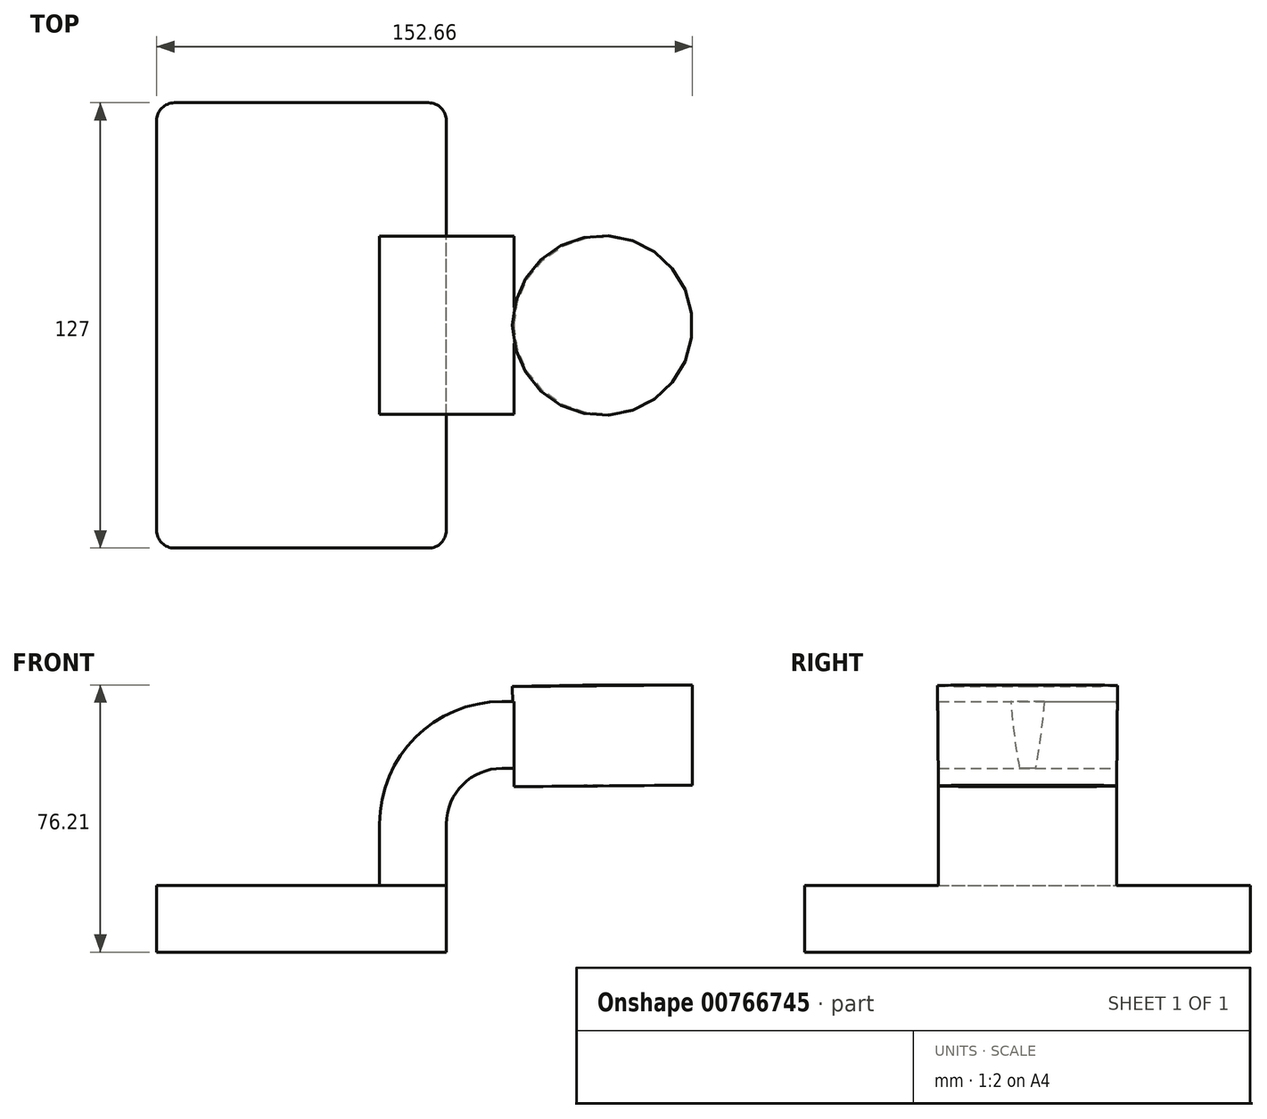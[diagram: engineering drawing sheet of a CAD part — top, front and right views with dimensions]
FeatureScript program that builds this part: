
annotation { "Feature Type Name" : "Feature", "Feature Type Description" : "" }
export const myFeature = defineFeature(function(context is Context, id is Id, definition is map)
    precondition{}
    {
        {
            var Q0;
            Q0=qCreatedBy(makeId("Front.planeOp"),FACE);
            var sketch = newSketch(context, id + "F0", { "sketchPlane" : qUnion([Q0])});
            skLineSegment(sketch, "E0.bottom", {"start": v(-41.28, 9.52) * mm, "end": v(41.27, 9.53) * mm});
            skLineSegment(sketch, "E0.top", {"start": v(-41.28, -9.53) * mm, "end": v(41.28, -9.53) * mm});
            skLineSegment(sketch, "E0.left", {"start": v(-41.28, 9.52) * mm, "end": v(-41.28, -9.53) * mm});
            skLineSegment(sketch, "E0.right", {"start": v(41.27, 9.53) * mm, "end": v(41.28, -9.52) * mm});
            skPoint(sketch, "E0.middle", {"position": v(0, 0) * mm});
            skLineSegment(sketch, "E1.bottom", {"start": v(111.39, 38.1) * mm, "end": v(60.59, 38.1) * mm});
            skLineSegment(sketch, "E1.top", {"start": v(111.39, 66.68) * mm, "end": v(60.59, 66.68) * mm});
            skLineSegment(sketch, "E1.left", {"start": v(111.39, 38.1) * mm, "end": v(111.39, 66.68) * mm});
            skLineSegment(sketch, "E1.right", {"start": v(60.59, 38.1) * mm, "end": v(60.59, 66.68) * mm});
            skPoint(sketch, "E1.middle", {"position": v(85.99, 52.39) * mm});
            skLineSegment(sketch, "E2", {"start": v(41.27, 9.53) * mm, "end": v(41.27, 27) * mm});
            skArc(sketch, "E3", {"start": v(41.27, 27) * mm, "mid": v(45.92, 38.23) * mm, "end": v(57.15, 42.88) * mm});
            skLineSegment(sketch, "E4", {"start": v(57.15, 42.88) * mm, "end": v(85.72, 42.88) * mm});
            skLineSegment(sketch, "E5.0", {"start": v(57.15, 61.93) * mm, "end": v(85.72, 61.93) * mm});
            skArc(sketch, "E5.1", {"start": v(22.22, 27) * mm, "mid": v(32.45, 51.7) * mm, "end": v(57.15, 61.93) * mm});
            skLineSegment(sketch, "E5.2", {"start": v(22.22, 9.53) * mm, "end": v(22.22, 27) * mm});
            skLineSegment(sketch, "E6", {"start": v(85.99, 38.1) * mm, "end": v(85.72, 66.68) * mm});
            skFitSpline(sketch, "E7", {"points": [v(-41.28, 9.52) * mm, v(57.15, 61.93) * mm], "startDerivative": vector(41.8, 115.77) * mm, "endDerivative": vector(181.9, -4.99) * mm});
            skSolve(sketch);
        }
        {
            var Q0;
            Q0=makeQuery(id+"F0.imprint","IMPRINT",FACE,{"disambiguationData":[TD([[makeQuery(id+"F0.imprint","IMPRINT",EDGE,{"derivedFrom":sQuery(id+"F0.wireOp",EDGE,"E0.top")}),1.0]])]});
            extrude(context, id + "F1", {"entities" : qUnion([Q0]), "endBound" : BoundingType.SYMMETRIC, "depth" : 127 * mm, "offsetDistance" : 25.4 * mm});
        }
        {
            var Q0;
            {var subQ1=sQuery(id+"F0.wireOp",EDGE,"E2");Q0=makeQuery(id+"F0.imprint","IMPRINT",FACE,{"disambiguationData":[TD([[makeQuery(id+"F0.imprint","IMPRINT",EDGE,{"derivedFrom":subQ1}),1.0]])]});}
            extrude(context, id + "F2", {"entities" : qUnion([Q0]), "operationType" : NewBodyOperationType.ADD, "endBound" : BoundingType.SYMMETRIC, "depth" : 50.8 * mm, "offsetDistance" : 25.4 * mm});
        }
        {
            var Q0;
            Q0=makeQuery(id+"F0.imprint","IMPRINT",FACE,{"disambiguationData":[TD([[makeQuery(id+"F0.imprint","IMPRINT",EDGE,{"derivedFrom":sQuery(id+"F0.wireOp",EDGE,"E5.1")}),1.0]])]});
            extrude(context, id + "F3", {"entities" : qUnion([Q0]), "operationType" : NewBodyOperationType.ADD, "endBound" : BoundingType.SYMMETRIC, "depth" : 15.88 * mm, "offsetDistance" : 25.4 * mm});
        }
        {
            var Q0;
            {var subQ0=sQuery(id+"F0.wireOp",EDGE,"E1.left");Q0=makeQuery(id+"F0.imprint","IMPRINT",FACE,{"disambiguationData":[TD([[makeQuery(id+"F0.imprint","IMPRINT",EDGE,{"derivedFrom":subQ0}),1.0]])]});}
            var Q1;
            Q1=sQuery(id+"F0.wireOp",EDGE,"E6");
            revolve(context, id + "F4", {"operationType" : NewBodyOperationType.ADD, "surfaceOperationType" : NewSurfaceOperationType.NEW, "entities" : qUnion([Q0]), "axis" : qUnion([Q1]), "revolveType" : RevolveType.FULL});
        }
        {
            var Q0;
            Q0=makeQuery(id+"F1.opExtrude","CAP_EDGE",EDGE,{"disambiguationData":[OSD([sQuery(id+"F0.wireOp",EDGE,"E0.right")])],"isStart":false});
            var Q1;
            Q1=makeQuery(id+"F1.opExtrude","CAP_EDGE",EDGE,{"disambiguationData":[OSD([sQuery(id+"F0.wireOp",EDGE,"E0.left")])],"isStart":false});
            var Q2;
            Q2=makeQuery(id+"F1.opExtrude","CAP_EDGE",EDGE,{"disambiguationData":[OSD([sQuery(id+"F0.wireOp",EDGE,"E0.right")])],"isStart":true});
            var Q3;
            Q3=makeQuery(id+"F1.opExtrude","CAP_EDGE",EDGE,{"disambiguationData":[OSD([sQuery(id+"F0.wireOp",EDGE,"E0.left")])],"isStart":true});
            fillet(context, id + "F5", {"entities" : qUnion([Q0, Q1, Q2, Q3]), "radius" : 5.08 * mm, "tangentPropagation" : true, "allowEdgeOverflow" : false});
        }
    });
